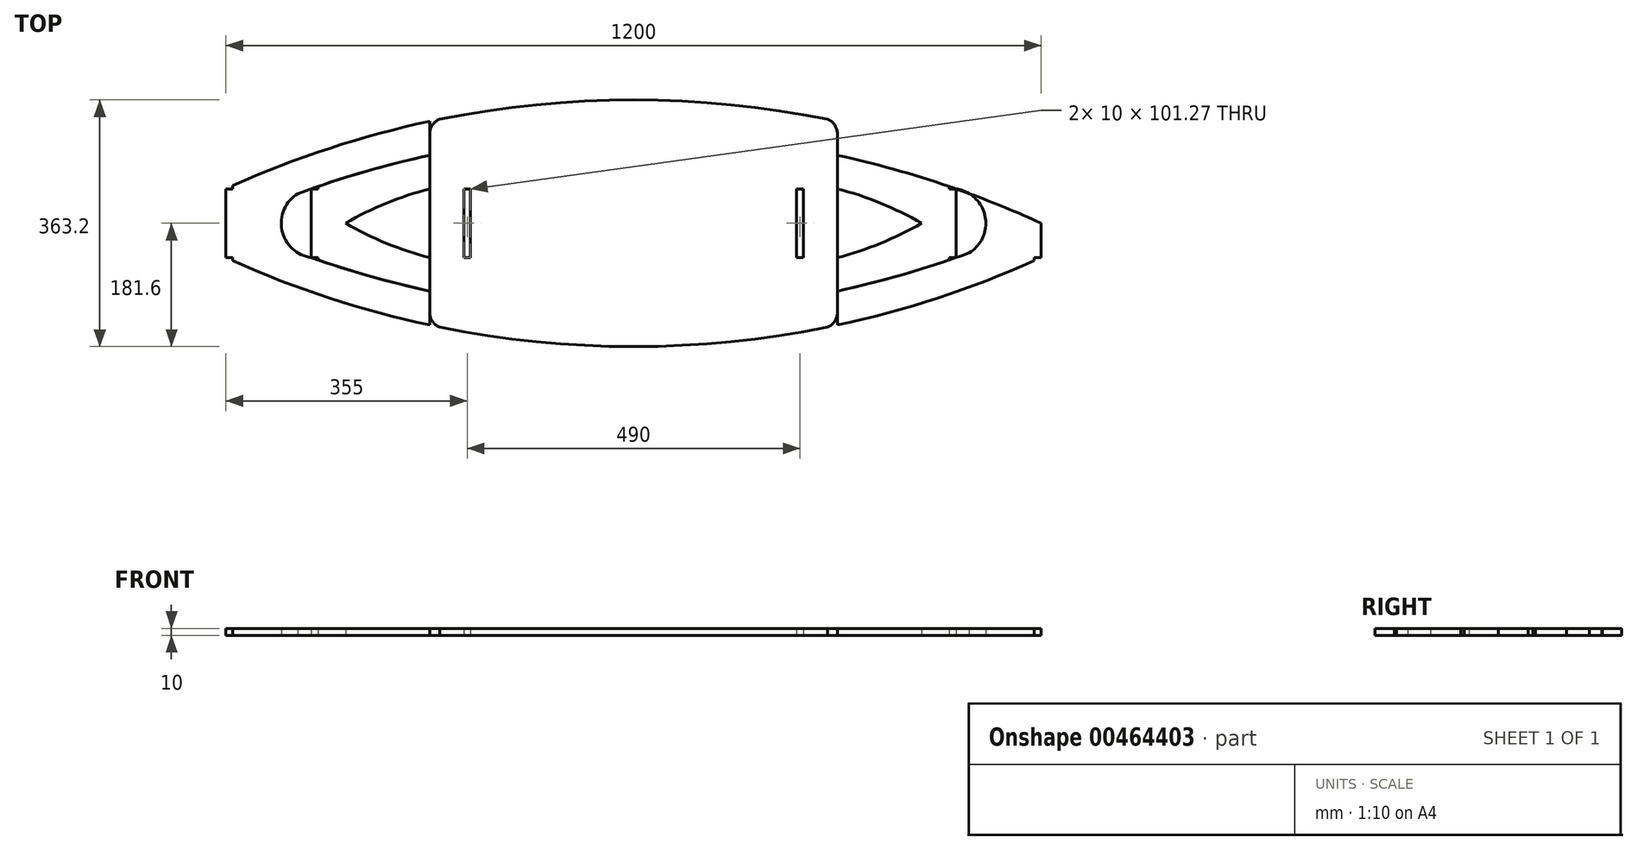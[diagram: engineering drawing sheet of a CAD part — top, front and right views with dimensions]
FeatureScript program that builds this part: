
annotation { "Feature Type Name" : "Feature", "Feature Type Description" : "" }
export const myFeature = defineFeature(function(context is Context, id is Id, definition is map)
    precondition{}
    {
        {
            var Q0;
            Q0=qCreatedBy(makeId("Top.planeOp"),FACE);
            var sketch = newSketch(context, id + "F0", { "sketchPlane" : qUnion([Q0])});
            skLineSegment(sketch, "E0", {"start": v(-1628.52, 0) * mm, "end": v(1582.02, 0) * mm, "construction": true});
            skLineSegment(sketch, "E1", {"start": v(0, 1146) * mm, "end": v(0, -696.99) * mm, "construction": true});
            skLineSegment(sketch, "E2.bottom", {"start": v(300, 150) * mm, "end": v(-300, 150) * mm, "construction": true});
            skLineSegment(sketch, "E2.top", {"start": v(300, -150) * mm, "end": v(-300, -150) * mm, "construction": true});
            skLineSegment(sketch, "E2.left", {"start": v(300, 150) * mm, "end": v(300, -150) * mm});
            skLineSegment(sketch, "E2.right", {"start": v(-300, 150) * mm, "end": v(-300, -150) * mm});
            skPoint(sketch, "E2.middle", {"position": v(0, 0) * mm});
            skCircle(sketch, "E3", {"center": v(0, -1258.33) * mm, "radius": 1439.93 * mm});
            skPoint(sketch, "E3.first.point", {"position": v(-700, 0) * mm});
            skCircle(sketch, "E4", {"center": v(0, 1258.33) * mm, "radius": 1439.93 * mm});
            skLineSegment(sketch, "E5", {"start": v(-600, 50.64) * mm, "end": v(-487.72, 50.64) * mm, "construction": true});
            skLineSegment(sketch, "E6", {"start": v(-600, -50.64) * mm, "end": v(600, -50.64) * mm, "construction": true});
            skLineSegment(sketch, "E7", {"start": v(-250, 50.64) * mm, "end": v(-250, -50.64) * mm});
            skLineSegment(sketch, "E8", {"start": v(-250, 50.64) * mm, "end": v(-240, 50.64) * mm});
            skLineSegment(sketch, "E9", {"start": v(-240, 50.64) * mm, "end": v(-240, -50.64) * mm});
            skLineSegment(sketch, "E10", {"start": v(-240, -50.64) * mm, "end": v(-250, -50.64) * mm});
            skLineSegment(sketch, "E11", {"start": v(-300, 150) * mm, "end": v(-300, 100) * mm, "construction": true});
            skArc(sketch, "E12", {"start": v(-300, 100) * mm, "mid": v(-452.7, 58.09) * mm, "end": v(-600, 0) * mm});
            skArc(sketch, "E13.MirrorCS", {"start": v(-300, -100) * mm, "mid": v(-452.7, -58.09) * mm, "end": v(-600, 0) * mm});
            skArc(sketch, "E14.MirrorCS", {"start": v(300, 100) * mm, "mid": v(452.7, 58.09) * mm, "end": v(600, 0) * mm});
            skArc(sketch, "E15.MirrorCS", {"start": v(300, -100) * mm, "mid": v(452.7, -58.09) * mm, "end": v(600, 0) * mm});
            skLineSegment(sketch, "E16.MirrorCS", {"start": v(250, 50.64) * mm, "end": v(240, 50.64) * mm});
            skLineSegment(sketch, "E17.MirrorCS", {"start": v(240, -50.64) * mm, "end": v(250, -50.64) * mm});
            skLineSegment(sketch, "E18.MirrorCS", {"start": v(240, 50.64) * mm, "end": v(240, -50.64) * mm});
            skLineSegment(sketch, "E19.MirrorCS", {"start": v(250, 50.64) * mm, "end": v(250, -50.64) * mm});
            skLineSegment(sketch, "E20", {"start": v(-590, 50.64) * mm, "end": v(-590, -50.64) * mm, "construction": true});
            skLineSegment(sketch, "E21", {"start": v(-600, 50.64) * mm, "end": v(-590, 50.64) * mm});
            skLineSegment(sketch, "E22", {"start": v(-590, 55.17) * mm, "end": v(-590, 50.64) * mm});
            skLineSegment(sketch, "E23", {"start": v(-600, -50.64) * mm, "end": v(-590, -50.64) * mm});
            skLineSegment(sketch, "E24", {"start": v(-590, -50.64) * mm, "end": v(-590, -55.17) * mm});
            skLineSegment(sketch, "E25.MirrorCS", {"start": v(600, -50.64) * mm, "end": v(590, -50.64) * mm});
            skLineSegment(sketch, "E26.MirrorCS", {"start": v(590, -50.64) * mm, "end": v(590, -55.17) * mm});
            skLineSegment(sketch, "E27.MirrorCS", {"start": v(590, 55.17) * mm, "end": v(590, 50.64) * mm});
            skLineSegment(sketch, "E28.MirrorCS", {"start": v(600, 50.64) * mm, "end": v(590, 50.64) * mm});
            skArc(sketch, "E29", {"start": v(-300, 50.64) * mm, "mid": v(-363.75, 29.55) * mm, "end": v(-424.06, 0) * mm});
            skArc(sketch, "E30.MirrorCS", {"start": v(-300, -50.64) * mm, "mid": v(-363.75, -29.55) * mm, "end": v(-424.06, 0) * mm});
            skArc(sketch, "E31.MirrorCS", {"start": v(300, 50.64) * mm, "mid": v(363.75, 29.55) * mm, "end": v(424.06, 0) * mm});
            skArc(sketch, "E32.MirrorCS", {"start": v(300, -50.64) * mm, "mid": v(363.75, -29.55) * mm, "end": v(424.06, 0) * mm});
            skLineSegment(sketch, "E33", {"start": v(-474.47, 50.64) * mm, "end": v(-464.47, 50.64) * mm});
            skLineSegment(sketch, "E34.trimOffspring", {"start": v(-474.47, 50.64) * mm, "end": v(600, 50.64) * mm, "construction": true});
            skLineSegment(sketch, "E35", {"start": v(-464.47, 50.64) * mm, "end": v(-464.47, 67.59) * mm});
            skLineSegment(sketch, "E36.MirrorCS", {"start": v(-464.47, -50.64) * mm, "end": v(-464.47, -67.59) * mm});
            skLineSegment(sketch, "E37.MirrorCS", {"start": v(-474.47, -50.64) * mm, "end": v(-464.47, -50.64) * mm});
            skLineSegment(sketch, "E38.MirrorCS", {"start": v(464.47, -50.64) * mm, "end": v(464.47, -67.59) * mm});
            skLineSegment(sketch, "E39.MirrorCS", {"start": v(474.47, 50.64) * mm, "end": v(464.47, 50.64) * mm});
            skLineSegment(sketch, "E40.MirrorCS", {"start": v(474.47, -50.64) * mm, "end": v(464.47, -50.64) * mm});
            skLineSegment(sketch, "E41.MirrorCS", {"start": v(464.47, 50.64) * mm, "end": v(464.47, 67.59) * mm});
            skLineSegment(sketch, "E42", {"start": v(-474.47, 50.64) * mm, "end": v(-474.47, -50.64) * mm});
            skArc(sketch, "E43", {"start": v(-474.47, 50.64) * mm, "mid": v(-518.5, 0) * mm, "end": v(-474.47, -50.64) * mm});
            skLineSegment(sketch, "E44", {"start": v(-600, 50.64) * mm, "end": v(-600, -50.64) * mm});
            skLineSegment(sketch, "E45.MirrorCS", {"start": v(600, 50.64) * mm, "end": v(600, -50.64) * mm});
            skLineSegment(sketch, "E46.MirrorCS", {"start": v(474.47, 50.64) * mm, "end": v(474.47, -50.64) * mm});
            skArc(sketch, "E47.MirrorCS", {"start": v(474.47, 50.64) * mm, "mid": v(518.5, 0) * mm, "end": v(474.47, -50.64) * mm});
            skArc(sketch, "E48", {"start": v(-285.46, 153.02) * mm, "mid": v(-295.5, 145.46) * mm, "end": v(-300, 133.74) * mm});
            skArc(sketch, "E49.MirrorCS", {"start": v(-285.46, -153.02) * mm, "mid": v(-295.5, -145.46) * mm, "end": v(-300, -133.74) * mm});
            skArc(sketch, "E50.MirrorCS", {"start": v(285.46, -153.02) * mm, "mid": v(295.5, -145.46) * mm, "end": v(300, -133.74) * mm});
            skArc(sketch, "E51.MirrorCS", {"start": v(285.46, 153.02) * mm, "mid": v(295.5, 145.46) * mm, "end": v(300, 133.74) * mm});
            skSolve(sketch);
        }
        {
            var Q0;
            {var subQ10=sQuery(id+"F0.wireOp",EDGE,"E14.MirrorCS");Q0=makeQuery(id+"F0.imprint","IMPRINT",FACE,{"disambiguationData":[TD([[makeQuery(id+"F0.imprint","IMPRINT",EDGE,{"derivedFrom":subQ10}),1.0]])]});}
            var Q1;
            {var subQ5=sQuery(id+"F0.wireOp",EDGE,"E12");Q1=makeQuery(id+"F0.imprint","IMPRINT",FACE,{"disambiguationData":[TD([[makeQuery(id+"F0.imprint","IMPRINT",EDGE,{"derivedFrom":subQ5}),-1.0]])]});}
            var Q2;
            {var subQ1=sQuery(id+"F0.wireOp",EDGE,"E12");var subQ3=sQuery(id+"F0.wireOp",EDGE,"E43");var subQ4=makeQuery(id+"F0.imprint","INTERSECT",VERTEX,{"derivedFrom":[subQ1,subQ3]});Q2=makeQuery(id+"F0.imprint","IMPRINT",FACE,{"disambiguationData":[TD([[makeQuery(id+"F0.imprint","IMPRINT",EDGE,{"disambiguationData":[TD([[subQ4,-1.0]])],"derivedFrom":subQ3}),-1.0]])]});}
            var Q3;
            {var subQ12=sQuery(id+"F0.wireOp",EDGE,"E23");Q3=makeQuery(id+"F0.imprint","IMPRINT",FACE,{"disambiguationData":[TD([[makeQuery(id+"F0.imprint","IMPRINT",EDGE,{"derivedFrom":subQ12}),1.0]])]});}
            var Q4;
            {var subQ0=sQuery(id+"F0.wireOp",EDGE,"E43");var subQ1=sQuery(id+"F0.wireOp",EDGE,"E12");var subQ3=makeQuery(id+"F0.imprint","INTERSECT",VERTEX,{"derivedFrom":[subQ1,subQ0]});Q4=makeQuery(id+"F0.imprint","IMPRINT",FACE,{"disambiguationData":[TD([[makeQuery(id+"F0.imprint","IMPRINT",EDGE,{"disambiguationData":[TD([[subQ3,1.0]])],"derivedFrom":subQ1}),-1.0]])]});}
            var Q5;
            {var subQ0=sQuery(id+"F0.wireOp",EDGE,"E43");var subQ1=sQuery(id+"F0.wireOp",EDGE,"E13.MirrorCS");var subQ3=makeQuery(id+"F0.imprint","INTERSECT",VERTEX,{"derivedFrom":[subQ1,subQ0]});Q5=makeQuery(id+"F0.imprint","IMPRINT",FACE,{"disambiguationData":[TD([[makeQuery(id+"F0.imprint","IMPRINT",EDGE,{"disambiguationData":[TD([[subQ3,1.0]])],"derivedFrom":subQ1}),1.0]])]});}
            var Q6;
            {var subQ4=sQuery(id+"F0.wireOp",EDGE,"E25.MirrorCS");Q6=makeQuery(id+"F0.imprint","IMPRINT",FACE,{"disambiguationData":[TD([[makeQuery(id+"F0.imprint","IMPRINT",EDGE,{"derivedFrom":subQ4}),-1.0]])]});}
            var Q7;
            {var subQ1=sQuery(id+"F0.wireOp",EDGE,"E14.MirrorCS");var subQ3=sQuery(id+"F0.wireOp",EDGE,"E47.MirrorCS");var subQ4=makeQuery(id+"F0.imprint","INTERSECT",VERTEX,{"derivedFrom":[subQ1,subQ3]});Q7=makeQuery(id+"F0.imprint","IMPRINT",FACE,{"disambiguationData":[TD([[makeQuery(id+"F0.imprint","IMPRINT",EDGE,{"disambiguationData":[TD([[subQ4,-1.0]])],"derivedFrom":subQ3}),1.0]])]});}
            var Q8;
            {var subQ0=sQuery(id+"F0.wireOp",EDGE,"E47.MirrorCS");var subQ1=sQuery(id+"F0.wireOp",EDGE,"E15.MirrorCS");var subQ3=makeQuery(id+"F0.imprint","INTERSECT",VERTEX,{"derivedFrom":[subQ1,subQ0]});Q8=makeQuery(id+"F0.imprint","IMPRINT",FACE,{"disambiguationData":[TD([[makeQuery(id+"F0.imprint","IMPRINT",EDGE,{"disambiguationData":[TD([[subQ3,1.0]])],"derivedFrom":subQ1}),-1.0]])]});}
            var Q9;
            {var subQ0=sQuery(id+"F0.wireOp",EDGE,"E47.MirrorCS");var subQ1=sQuery(id+"F0.wireOp",EDGE,"E14.MirrorCS");var subQ3=makeQuery(id+"F0.imprint","INTERSECT",VERTEX,{"derivedFrom":[subQ1,subQ0]});Q9=makeQuery(id+"F0.imprint","IMPRINT",FACE,{"disambiguationData":[TD([[makeQuery(id+"F0.imprint","IMPRINT",EDGE,{"disambiguationData":[TD([[subQ3,1.0]])],"derivedFrom":subQ1}),1.0]])]});}
            extrude(context, id + "F1", {"entities" : qUnion([Q0, Q1, Q2, Q3, Q4, Q5, Q6, Q7, Q8, Q9]), "depth" : 10 * mm});
        }
        {
            var Q0;
            Q0=makeQuery(id+"F0.imprint","IMPRINT",FACE,{"disambiguationData":[TD([[makeQuery(id+"F0.imprint","IMPRINT",EDGE,{"derivedFrom":sQuery(id+"F0.wireOp",EDGE,"E7")}),-1.0]])]});
            extrude(context, id + "F2", {"entities" : qUnion([Q0]), "depth" : 10 * mm});
        }
        {
            var Q0;
            {var subQ6=sQuery(id+"F0.wireOp",EDGE,"E29");Q0=makeQuery(id+"F0.imprint","IMPRINT",FACE,{"disambiguationData":[TD([[makeQuery(id+"F0.imprint","IMPRINT",EDGE,{"derivedFrom":subQ6}),-1.0]])]});}
            var Q1;
            {var subQ2=sQuery(id+"F0.wireOp",EDGE,"E39.MirrorCS");Q1=makeQuery(id+"F0.imprint","IMPRINT",FACE,{"disambiguationData":[TD([[makeQuery(id+"F0.imprint","IMPRINT",EDGE,{"derivedFrom":subQ2}),1.0]])]});}
            extrude(context, id + "F3", {"entities" : qUnion([Q0, Q1]), "depth" : 10 * mm});
        }
    });
